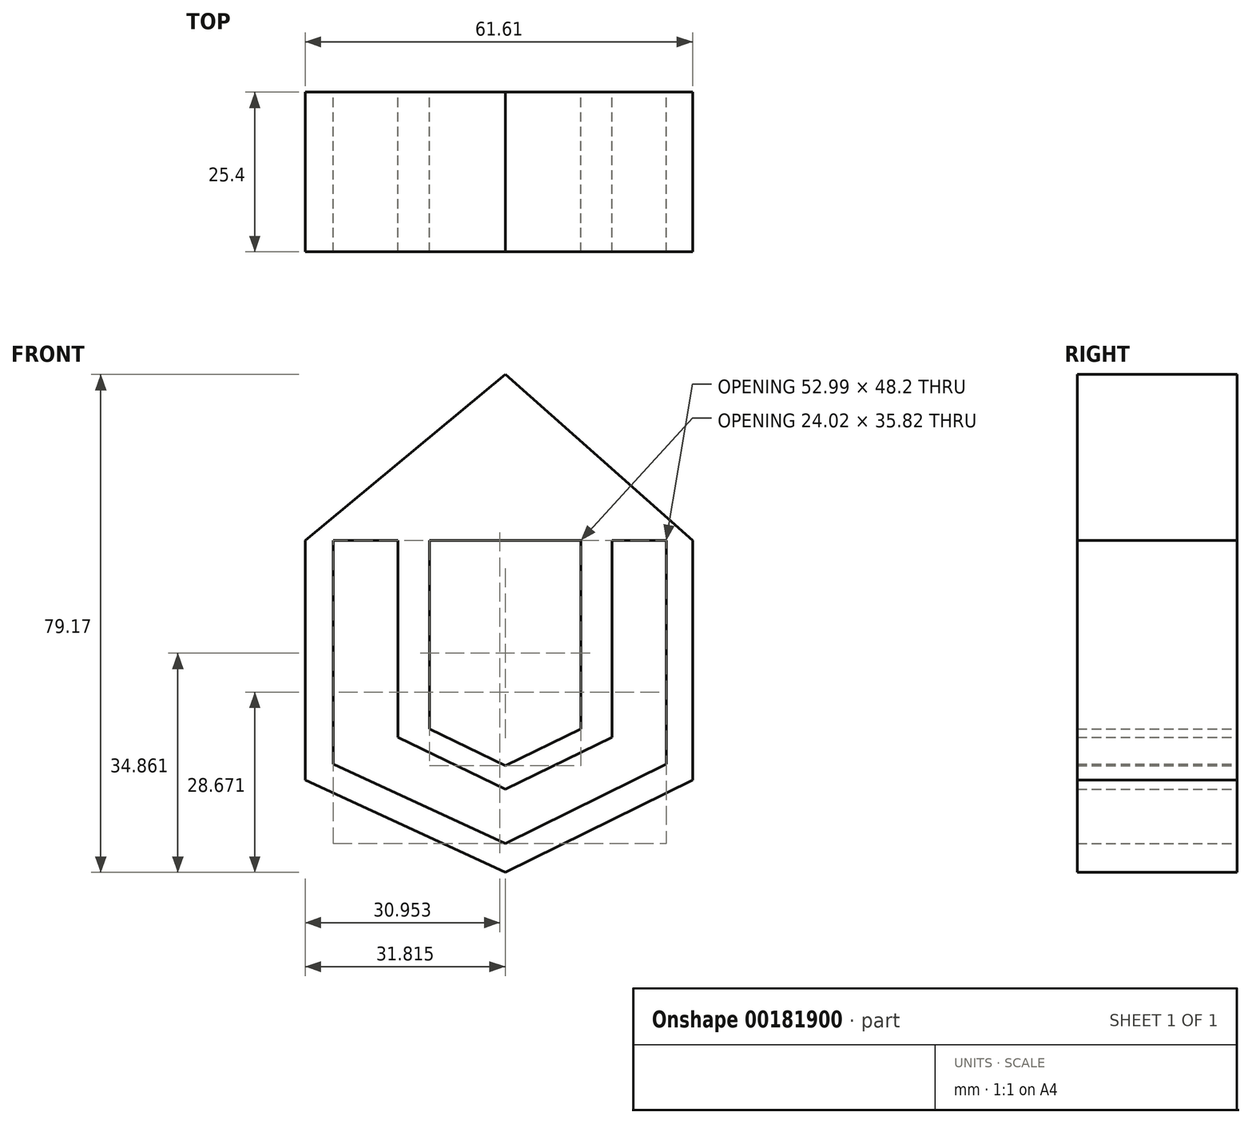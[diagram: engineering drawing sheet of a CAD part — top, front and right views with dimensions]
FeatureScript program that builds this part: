
annotation { "Feature Type Name" : "Feature", "Feature Type Description" : "" }
export const myFeature = defineFeature(function(context is Context, id is Id, definition is map)
    precondition{}
    {
        {
            var Q0;
            Q0=qCreatedBy(makeId("Front.planeOp"),FACE);
            var sketch = newSketch(context, id + "F0", { "sketchPlane" : qUnion([Q0])});
            skLineSegment(sketch, "E0", {"start": v(0, 28.44) * mm, "end": v(-31.86, 28.44) * mm});
            skLineSegment(sketch, "E1", {"start": v(0, 28.44) * mm, "end": v(29.75, 28.44) * mm});
            skLineSegment(sketch, "E2", {"start": v(-31.86, 28.44) * mm, "end": v(-31.86, -9.66) * mm});
            skLineSegment(sketch, "E3", {"start": v(-31.86, -9.66) * mm, "end": v(0, -24.33) * mm});
            skLineSegment(sketch, "E4", {"start": v(0, -24.33) * mm, "end": v(29.75, -9.66) * mm});
            skLineSegment(sketch, "E5", {"start": v(29.75, -9.66) * mm, "end": v(29.75, 28.44) * mm});
            skLineSegment(sketch, "E6", {"start": v(-31.86, 28.44) * mm, "end": v(29.75, 28.44) * mm});
            skLineSegment(sketch, "E7", {"start": v(-27.4, 28.44) * mm, "end": v(-27.4, -7.14) * mm});
            skLineSegment(sketch, "E8", {"start": v(-27.4, -7.14) * mm, "end": v(0, -19.76) * mm});
            skLineSegment(sketch, "E9", {"start": v(0, -19.76) * mm, "end": v(25.6, -7.14) * mm});
            skLineSegment(sketch, "E10", {"start": v(25.6, -7.14) * mm, "end": v(25.6, 28.44) * mm});
            skLineSegment(sketch, "E11", {"start": v(-17.09, 28.44) * mm, "end": v(-17.09, -2.86) * mm});
            skLineSegment(sketch, "E12", {"start": v(-17.09, -2.86) * mm, "end": v(0, -11.12) * mm});
            skLineSegment(sketch, "E13", {"start": v(0, -11.12) * mm, "end": v(16.96, -2.86) * mm});
            skLineSegment(sketch, "E14", {"start": v(16.96, -2.86) * mm, "end": v(16.96, 28.44) * mm});
            skLineSegment(sketch, "E15", {"start": v(-12.06, 28.44) * mm, "end": v(-12.06, -1.55) * mm});
            skLineSegment(sketch, "E16", {"start": v(-12.06, -1.55) * mm, "end": v(0, -7.38) * mm});
            skLineSegment(sketch, "E17", {"start": v(0, -7.38) * mm, "end": v(11.97, -1.55) * mm});
            skLineSegment(sketch, "E18", {"start": v(11.97, -1.55) * mm, "end": v(11.97, 28.44) * mm});
            skLineSegment(sketch, "E19", {"start": v(-31.86, 28.44) * mm, "end": v(0, 54.84) * mm});
            skLineSegment(sketch, "E20", {"start": v(0, 54.84) * mm, "end": v(29.75, 28.44) * mm});
            skSolve(sketch);
        }
        {
            var Q0;
            Q0 = qSketchRegion(id + "F0", true);
            var Q1;
            {var subQ0=sQuery(id+"F0.wireOp",EDGE,"E11");Q1=makeQuery(id+"F0.imprint","IMPRINT",FACE,{"disambiguationData":[TD([[makeQuery(id+"F0.imprint","IMPRINT",EDGE,{"derivedFrom":subQ0}),1.0]])]});}
            extrude(context, id + "F1", {"entities" : qUnion([Q0, Q1]), "depth" : 25.4 * mm});
        }
    });
